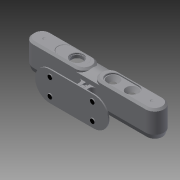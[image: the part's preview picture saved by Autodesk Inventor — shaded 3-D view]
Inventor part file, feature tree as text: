
AUTODESK INVENTOR PART (.ipt)
format: ipt  version: 2013 (Build 170138000, 138)  size: 465,408 bytes
history: native  units: mm
features: extrude x13, chamfer x13, sketch x13, fillet x9, other x3
ambient origin geometry x8: Origin, YZ Plane, XZ Plane, XY Plane, X Axis, Y Axis, Z Axis, Center Point
feature tree (51):
  other  "ソリッド1"
  extrude  "押し出し1"  Depth=25.0mm
  chamfer  "面取り1"  Distance=12.5mm
  extrude  "押し出し6"  Depth=25.0mm
  chamfer  "面取り7"  Distance=154.0mm
  chamfer  "面取り9"  Distance=79.0mm
  fillet  "フィレット4"  Radius=34.5mm
  chamfer  "面取り11"  Distance=2.0mm Angle=45.0deg
  fillet  "フィレット5"  Radius=57.5mm
  fillet  "フィレット6"  Radius=61.5mm
  chamfer  "面取り12"  Distance=12.5mm
  extrude  "押し出し7"  Depth=12.5mm
  extrude  "押し出し8"  Depth=1.5mm TaperAngle=0.0deg
  chamfer  "面取り13"  Distance=1.5mm Angle=45.0deg
  fillet  "フィレット7"  Radius=1.5mm
  chamfer  "面取り14"  Distance=15.0mm
  extrude  "押し出し9"  Depth=2.5mm TaperAngle=30.0deg
  chamfer  "面取り15"  Distance=40.0mm
  chamfer  "面取り16"  Distance=12.0mm
  extrude  "押し出し10"  Depth=2.5mm TaperAngle=30.0deg
  extrude  "押し出し11"  Depth=19.0mm
  chamfer  "面取り17"  Distance=10.0mm
  fillet  "フィレット8"  Radius=10.0mm
  extrude  "押し出し12"  Depth=22.0mm
  fillet  "フィレット9"  Radius=22.0mm
  extrude  "押し出し13"  Depth=10.0mm
  chamfer  "面取り18"  Distance=10.0mm
  extrude  "押し出し14"  Depth=3.5mm
  chamfer  "面取り19"  Distance=3.5mm
  extrude  "押し出し15"  Depth=4.0mm
  fillet  "フィレット10"  Radius=0.5mm
  extrude  "押し出し16"  Depth=18.0mm
  fillet  "フィレット11"  Radius=10.0mm
  chamfer  "面取り21"  Distance=10.0mm
  extrude  "押し出し17"  Depth=26.0mm
  fillet  "フィレット12"  Radius=22.0mm
  sketch  "スケッチ1"
  sketch  "スケッチ7"
  sketch  "スケッチ8"
  sketch  "スケッチ10"
  sketch  "スケッチ11"
  sketch  "スケッチ12"
  sketch  "スケッチ13"
  sketch  "スケッチ14"
  sketch  "スケッチ15"
  sketch  "スケッチ16"
  sketch  "スケッチ17"
  sketch  "スケッチ18"
  sketch  "スケッチ19"
  other  "断面エッジを投影1"
  other  "断面エッジを投影2"
